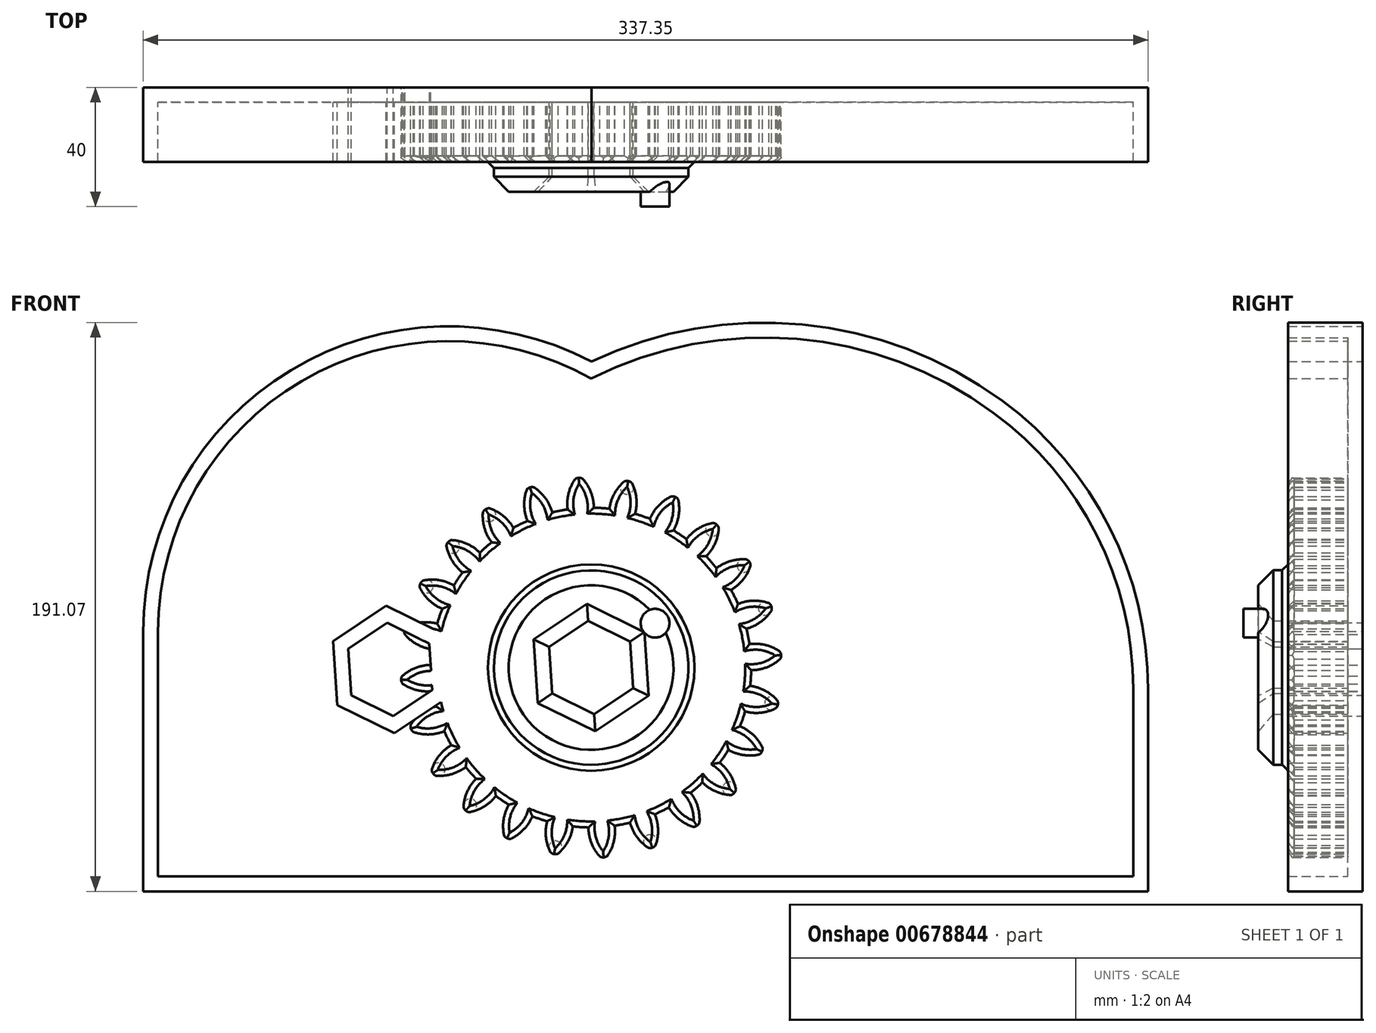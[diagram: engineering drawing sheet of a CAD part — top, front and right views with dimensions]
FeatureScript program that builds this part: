
annotation { "Feature Type Name" : "Feature", "Feature Type Description" : "" }
export const myFeature = defineFeature(function(context is Context, id is Id, definition is map)
    precondition{}
    {
        {
            var Q0;
            Q0=qCreatedBy(makeId("Front.planeOp"),FACE);
            var sketch = newSketch(context, id + "F0", { "sketchPlane" : qUnion([Q0])});
            skCircle(sketch, "E0", {"center": v(0, 0) * mm, "radius": 53.72 * mm});
            skCircle(sketch, "E1", {"center": v(0, 0) * mm, "radius": 58.67 * mm, "construction": true});
            skCircle(sketch, "E2", {"center": v(0, 0) * mm, "radius": 63.5 * mm, "construction": true});
            skLineSegment(sketch, "E3", {"start": v(0, 0) * mm, "end": v(0, 75.2) * mm, "construction": true});
            skLineSegment(sketch, "E4", {"start": v(0, 0) * mm, "end": v(-5.34, 81.5) * mm, "construction": true});
            skLineSegment(sketch, "E5", {"start": v(0, 58.67) * mm, "end": v(-72.87, 58.67) * mm, "construction": true});
            skLineSegment(sketch, "E6", {"start": v(0, 58.67) * mm, "end": v(-71.24, 32.75) * mm, "construction": true});
            skCircle(sketch, "E7", {"center": v(0, 0) * mm, "radius": 55.14 * mm, "construction": true});
            skCircle(sketch, "E8", {"center": v(0, 58.67) * mm, "radius": 14.6 * mm, "construction": true});
            skCircle(sketch, "E9", {"center": v(-13.72, 53.68) * mm, "radius": 14.6 * mm, "construction": true});
            skArc(sketch, "E10", {"start": v(0, 58.67) * mm, "mid": v(-1.2, 61.2) * mm, "end": v(-2.86, 63.44) * mm});
            skArc(sketch, "E11", {"start": v(0.88, 53.71) * mm, "mid": v(0.66, 56.23) * mm, "end": v(0, 58.67) * mm});
            skArc(sketch, "E12.MirrorCS", {"start": v(-7.88, 53.14) * mm, "mid": v(-8, 55.67) * mm, "end": v(-7.66, 58.17) * mm});
            skArc(sketch, "E13.MirrorCS", {"start": v(-7.66, 58.17) * mm, "mid": v(-6.8, 60.82) * mm, "end": v(-5.45, 63.27) * mm});
            skArc(sketch, "E14", {"start": v(-2.86, 63.44) * mm, "mid": v(-4.18, 63.76) * mm, "end": v(-5.45, 63.27) * mm});
            skCircle(sketch, "E15", {"center": v(0, 0) * mm, "radius": 32.66 * mm});
            skCircle(sketch, "E16.cCircle", {"center": v(0, 0) * mm, "radius": 15.7 * mm, "construction": true});
            skLineSegment(sketch, "E16.0", {"start": v(-1.03, 15.66) * mm, "end": v(13.05, 8.72) * mm});
            skLineSegment(sketch, "E16.1", {"start": v(13.05, 8.72) * mm, "end": v(14.08, -6.94) * mm});
            skLineSegment(sketch, "E16.2", {"start": v(14.08, -6.94) * mm, "end": v(1.03, -15.66) * mm});
            skLineSegment(sketch, "E16.3", {"start": v(1.03, -15.66) * mm, "end": v(-13.05, -8.72) * mm});
            skLineSegment(sketch, "E16.4", {"start": v(-13.05, -8.72) * mm, "end": v(-14.08, 6.94) * mm});
            skLineSegment(sketch, "E16.5", {"start": v(-14.08, 6.94) * mm, "end": v(-1.03, 15.66) * mm});
            skSolve(sketch);
        }
        {
            var Q0;
            {var subQ0=sQuery(id+"F0.wireOp",EDGE,"E0");var subQ1=makeQuery(id+"F0.imprint","INTERSECT",VERTEX,{"derivedFrom":[subQ0,sQuery(id+"F0.wireOp",EDGE,"E11")]});Q0=makeQuery(id+"F0.imprint","IMPRINT",FACE,{"disambiguationData":[TD([[makeQuery(id+"F0.imprint","IMPRINT",EDGE,{"disambiguationData":[TD([[subQ1,-1.0]])],"derivedFrom":subQ0}),1.0]])]});}
            var Q1;
            Q1=makeQuery(id+"F0.imprint","IMPRINT",FACE,{"disambiguationData":[TD([[makeQuery(id+"F0.imprint","IMPRINT",EDGE,{"derivedFrom":sQuery(id+"F0.wireOp",EDGE,"E10")}),1.0]])]});
            extrude(context, id + "F1", {"entities" : qUnion([Q0, Q1]), "depth" : 25 * mm, "offsetDistance" : 25 * mm});
        }
        {
            var Q0;
            Q0=makeQuery(id+"F1.opExtrude","SWEPT_BODY",BODY,{"disambiguationData":[OSD([sQuery(id+"F0.wireOp",EDGE,"E0"),sQuery(id+"F0.wireOp",EDGE,"E10"),sQuery(id+"F0.wireOp",EDGE,"E11"),sQuery(id+"F0.wireOp",EDGE,"E12.MirrorCS"),sQuery(id+"F0.wireOp",EDGE,"E13.MirrorCS"),sQuery(id+"F0.wireOp",EDGE,"E14")])]});
            var Q1;
            Q1=makeQuery(id+"F1.opExtrude","SWEPT_FACE",FACE,{"disambiguationData":[OSD([sQuery(id+"F0.wireOp",EDGE,"E0")])]});
            circularPattern(context, id + "F2", {"entities" : qUnion([Q0]), "axis" : qUnion([Q1]), "angle" : 360 * degree, "instanceCount" : 24, "equalSpace" : true});
        }
        {
            var Q0;
            Q0=makeQuery(id+"F0.imprint","IMPRINT",FACE,{"disambiguationData":[TD([[makeQuery(id+"F0.imprint","IMPRINT",EDGE,{"derivedFrom":sQuery(id+"F0.wireOp",EDGE,"E15")}),1.0]])]});
            extrude(context, id + "F3", {"entities" : qUnion([Q0]), "operationType" : NewBodyOperationType.ADD, "depth" : 35 * mm, "offsetDistance" : 25 * mm});
        }
        {
            var Q0;
            Q0=makeQuery(id+"F3.opExtrude","CAP_FACE",FACE,{"disambiguationData":[OSD([sQuery(id+"F0.wireOp",EDGE,"E15"),sQuery(id+"F0.wireOp",EDGE,"E16.0"),sQuery(id+"F0.wireOp",EDGE,"E16.1"),sQuery(id+"F0.wireOp",EDGE,"E16.2"),sQuery(id+"F0.wireOp",EDGE,"E16.3"),sQuery(id+"F0.wireOp",EDGE,"E16.4"),sQuery(id+"F0.wireOp",EDGE,"E16.5")])],"isStart":false});
            chamfer(context, id + "F4", {"entities" : qUnion([Q0]), "width" : 5 * mm, "tangentPropagation" : true});
        }
        {
            var Q0;
            Q0=makeQuery(id+"F2.opPattern","COPY",EDGE,{"derivedFrom":makeQuery(id+"F1.opExtrude","CAP_EDGE",EDGE,{"disambiguationData":[OSD([sQuery(id+"F0.wireOp",EDGE,"E14")])],"isStart":false}),"instanceName":"21"});
            var Q1;
            Q1=makeQuery(id+"F2.opPattern","COPY",EDGE,{"derivedFrom":makeQuery(id+"F1.opExtrude","CAP_EDGE",EDGE,{"disambiguationData":[OSD([sQuery(id+"F0.wireOp",EDGE,"E10")])],"isStart":false}),"instanceName":"21"});
            var Q2;
            Q2=makeQuery(id+"F2.opPattern","COPY",EDGE,{"derivedFrom":makeQuery(id+"F1.opExtrude","CAP_EDGE",EDGE,{"disambiguationData":[OSD([sQuery(id+"F0.wireOp",EDGE,"E11")])],"isStart":false}),"instanceName":"21"});
            var Q3;
            Q3=makeQuery(id+"F2.opPattern","COPY",EDGE,{"derivedFrom":makeQuery(id+"F1.opExtrude","CAP_EDGE",EDGE,{"disambiguationData":[OSD([sQuery(id+"F0.wireOp",EDGE,"E13.MirrorCS")])],"isStart":false}),"instanceName":"21"});
            var Q4;
            Q4=makeQuery(id+"F2.opPattern","COPY",EDGE,{"derivedFrom":makeQuery(id+"F1.opExtrude","CAP_EDGE",EDGE,{"disambiguationData":[OSD([sQuery(id+"F0.wireOp",EDGE,"E12.MirrorCS")])],"isStart":false}),"instanceName":"21"});
            var Q5;
            Q5=makeQuery(id+"F1.opExtrude","CAP_EDGE",EDGE,{"disambiguationData":[OSD([sQuery(id+"F0.wireOp",EDGE,"E14")])],"isStart":false});
            var Q6;
            Q6=makeQuery(id+"F1.opExtrude","CAP_EDGE",EDGE,{"disambiguationData":[OSD([sQuery(id+"F0.wireOp",EDGE,"E13.MirrorCS")])],"isStart":false});
            var Q7;
            Q7=makeQuery(id+"F1.opExtrude","CAP_EDGE",EDGE,{"disambiguationData":[OSD([sQuery(id+"F0.wireOp",EDGE,"E10")])],"isStart":false});
            var Q8;
            Q8=makeQuery(id+"F1.opExtrude","CAP_EDGE",EDGE,{"disambiguationData":[OSD([sQuery(id+"F0.wireOp",EDGE,"E12.MirrorCS")])],"isStart":false});
            var Q9;
            Q9=makeQuery(id+"F1.opExtrude","CAP_EDGE",EDGE,{"disambiguationData":[OSD([sQuery(id+"F0.wireOp",EDGE,"E11")])],"isStart":false});
            var Q10;
            Q10=makeQuery(id+"F2.opPattern","COPY",EDGE,{"derivedFrom":makeQuery(id+"F1.opExtrude","CAP_EDGE",EDGE,{"disambiguationData":[OSD([sQuery(id+"F0.wireOp",EDGE,"E13.MirrorCS")])],"isStart":false}),"instanceName":"22"});
            var Q11;
            Q11=makeQuery(id+"F2.opPattern","COPY",EDGE,{"derivedFrom":makeQuery(id+"F1.opExtrude","CAP_EDGE",EDGE,{"disambiguationData":[OSD([sQuery(id+"F0.wireOp",EDGE,"E14")])],"isStart":false}),"instanceName":"22"});
            var Q12;
            Q12=makeQuery(id+"F2.opPattern","COPY",EDGE,{"derivedFrom":makeQuery(id+"F1.opExtrude","CAP_EDGE",EDGE,{"disambiguationData":[OSD([sQuery(id+"F0.wireOp",EDGE,"E12.MirrorCS")])],"isStart":false}),"instanceName":"22"});
            var Q13;
            Q13=makeQuery(id+"F2.opPattern","COPY",EDGE,{"derivedFrom":makeQuery(id+"F1.opExtrude","CAP_EDGE",EDGE,{"disambiguationData":[OSD([sQuery(id+"F0.wireOp",EDGE,"E10")])],"isStart":false}),"instanceName":"22"});
            var Q14;
            Q14=makeQuery(id+"F2.opPattern","COPY",EDGE,{"derivedFrom":makeQuery(id+"F1.opExtrude","CAP_EDGE",EDGE,{"disambiguationData":[OSD([sQuery(id+"F0.wireOp",EDGE,"E11")])],"isStart":false}),"instanceName":"22"});
            var Q15;
            Q15=makeQuery(id+"F2.opPattern","COPY",EDGE,{"derivedFrom":makeQuery(id+"F1.opExtrude","CAP_EDGE",EDGE,{"disambiguationData":[OSD([sQuery(id+"F0.wireOp",EDGE,"E13.MirrorCS")])],"isStart":false}),"instanceName":"23"});
            var Q16;
            Q16=makeQuery(id+"F2.opPattern","COPY",EDGE,{"derivedFrom":makeQuery(id+"F1.opExtrude","CAP_EDGE",EDGE,{"disambiguationData":[OSD([sQuery(id+"F0.wireOp",EDGE,"E14")])],"isStart":false}),"instanceName":"23"});
            var Q17;
            Q17=makeQuery(id+"F2.opPattern","COPY",EDGE,{"derivedFrom":makeQuery(id+"F1.opExtrude","CAP_EDGE",EDGE,{"disambiguationData":[OSD([sQuery(id+"F0.wireOp",EDGE,"E10")])],"isStart":false}),"instanceName":"23"});
            var Q18;
            Q18=makeQuery(id+"F2.opPattern","COPY",EDGE,{"derivedFrom":makeQuery(id+"F1.opExtrude","CAP_EDGE",EDGE,{"disambiguationData":[OSD([sQuery(id+"F0.wireOp",EDGE,"E11")])],"isStart":false}),"instanceName":"23"});
            var Q19;
            Q19=makeQuery(id+"F2.opPattern","COPY",EDGE,{"derivedFrom":makeQuery(id+"F1.opExtrude","CAP_EDGE",EDGE,{"disambiguationData":[OSD([sQuery(id+"F0.wireOp",EDGE,"E12.MirrorCS")])],"isStart":false}),"instanceName":"23"});
            var Q20;
            Q20=makeQuery(id+"F2.opPattern","COPY",EDGE,{"derivedFrom":makeQuery(id+"F1.opExtrude","CAP_EDGE",EDGE,{"disambiguationData":[OSD([sQuery(id+"F0.wireOp",EDGE,"E14")])],"isStart":false}),"instanceName":"20"});
            var Q21;
            Q21=makeQuery(id+"F2.opPattern","COPY",EDGE,{"derivedFrom":makeQuery(id+"F1.opExtrude","CAP_EDGE",EDGE,{"disambiguationData":[OSD([sQuery(id+"F0.wireOp",EDGE,"E10")])],"isStart":false}),"instanceName":"20"});
            var Q22;
            Q22=makeQuery(id+"F2.opPattern","COPY",EDGE,{"derivedFrom":makeQuery(id+"F1.opExtrude","CAP_EDGE",EDGE,{"disambiguationData":[OSD([sQuery(id+"F0.wireOp",EDGE,"E11")])],"isStart":false}),"instanceName":"20"});
            var Q23;
            Q23=makeQuery(id+"F2.opPattern","COPY",EDGE,{"derivedFrom":makeQuery(id+"F1.opExtrude","CAP_EDGE",EDGE,{"disambiguationData":[OSD([sQuery(id+"F0.wireOp",EDGE,"E13.MirrorCS")])],"isStart":false}),"instanceName":"20"});
            var Q24;
            Q24=makeQuery(id+"F2.opPattern","COPY",EDGE,{"derivedFrom":makeQuery(id+"F1.opExtrude","CAP_EDGE",EDGE,{"disambiguationData":[OSD([sQuery(id+"F0.wireOp",EDGE,"E12.MirrorCS")])],"isStart":false}),"instanceName":"20"});
            var Q25;
            Q25=makeQuery(id+"F2.opPattern","COPY",EDGE,{"derivedFrom":makeQuery(id+"F1.opExtrude","CAP_EDGE",EDGE,{"disambiguationData":[OSD([sQuery(id+"F0.wireOp",EDGE,"E10")])],"isStart":false}),"instanceName":"19"});
            var Q26;
            Q26=makeQuery(id+"F2.opPattern","COPY",EDGE,{"derivedFrom":makeQuery(id+"F1.opExtrude","CAP_EDGE",EDGE,{"disambiguationData":[OSD([sQuery(id+"F0.wireOp",EDGE,"E11")])],"isStart":false}),"instanceName":"19"});
            var Q27;
            Q27=makeQuery(id+"F2.opPattern","COPY",EDGE,{"derivedFrom":makeQuery(id+"F1.opExtrude","CAP_EDGE",EDGE,{"disambiguationData":[OSD([sQuery(id+"F0.wireOp",EDGE,"E14")])],"isStart":false}),"instanceName":"19"});
            var Q28;
            Q28=makeQuery(id+"F2.opPattern","COPY",EDGE,{"derivedFrom":makeQuery(id+"F1.opExtrude","CAP_EDGE",EDGE,{"disambiguationData":[OSD([sQuery(id+"F0.wireOp",EDGE,"E13.MirrorCS")])],"isStart":false}),"instanceName":"19"});
            var Q29;
            Q29=makeQuery(id+"F2.opPattern","COPY",EDGE,{"derivedFrom":makeQuery(id+"F1.opExtrude","CAP_EDGE",EDGE,{"disambiguationData":[OSD([sQuery(id+"F0.wireOp",EDGE,"E12.MirrorCS")])],"isStart":false}),"instanceName":"19"});
            var Q30;
            Q30=makeQuery(id+"F2.opPattern","COPY",EDGE,{"derivedFrom":makeQuery(id+"F1.opExtrude","CAP_EDGE",EDGE,{"disambiguationData":[OSD([sQuery(id+"F0.wireOp",EDGE,"E14")])],"isStart":false}),"instanceName":"18"});
            var Q31;
            Q31=makeQuery(id+"F2.opPattern","COPY",EDGE,{"derivedFrom":makeQuery(id+"F1.opExtrude","CAP_EDGE",EDGE,{"disambiguationData":[OSD([sQuery(id+"F0.wireOp",EDGE,"E13.MirrorCS")])],"isStart":false}),"instanceName":"18"});
            var Q32;
            Q32=makeQuery(id+"F2.opPattern","COPY",EDGE,{"derivedFrom":makeQuery(id+"F1.opExtrude","CAP_EDGE",EDGE,{"disambiguationData":[OSD([sQuery(id+"F0.wireOp",EDGE,"E12.MirrorCS")])],"isStart":false}),"instanceName":"18"});
            var Q33;
            Q33=makeQuery(id+"F2.opPattern","COPY",EDGE,{"derivedFrom":makeQuery(id+"F1.opExtrude","CAP_EDGE",EDGE,{"disambiguationData":[OSD([sQuery(id+"F0.wireOp",EDGE,"E10")])],"isStart":false}),"instanceName":"18"});
            var Q34;
            {var subQ0=makeQuery(id+"F1.opExtrude","CAP_FACE",FACE,{"disambiguationData":[OSD([sQuery(id+"F0.wireOp",EDGE,"E0"),sQuery(id+"F0.wireOp",EDGE,"E10"),sQuery(id+"F0.wireOp",EDGE,"E11"),sQuery(id+"F0.wireOp",EDGE,"E12.MirrorCS"),sQuery(id+"F0.wireOp",EDGE,"E13.MirrorCS"),sQuery(id+"F0.wireOp",EDGE,"E14"),sQuery(id+"F0.wireOp",EDGE,"E15")])],"isStart":false});Q34=makeQuery(id+"F3.boolean.opBoolean","MERGE",FACE,{"derivedFrom":[subQ0,makeQuery(id+"F2.opPattern","COPY",FACE,{"derivedFrom":subQ0,"instanceName":"1"}),makeQuery(id+"F2.opPattern","COPY",FACE,{"derivedFrom":subQ0,"instanceName":"2"}),makeQuery(id+"F2.opPattern","COPY",FACE,{"derivedFrom":subQ0,"instanceName":"3"}),makeQuery(id+"F2.opPattern","COPY",FACE,{"derivedFrom":subQ0,"instanceName":"4"}),makeQuery(id+"F2.opPattern","COPY",FACE,{"derivedFrom":subQ0,"instanceName":"5"}),makeQuery(id+"F2.opPattern","COPY",FACE,{"derivedFrom":subQ0,"instanceName":"6"}),makeQuery(id+"F2.opPattern","COPY",FACE,{"derivedFrom":subQ0,"instanceName":"7"}),makeQuery(id+"F2.opPattern","COPY",FACE,{"derivedFrom":subQ0,"instanceName":"8"}),makeQuery(id+"F2.opPattern","COPY",FACE,{"derivedFrom":subQ0,"instanceName":"9"}),makeQuery(id+"F2.opPattern","COPY",FACE,{"derivedFrom":subQ0,"instanceName":"10"}),makeQuery(id+"F2.opPattern","COPY",FACE,{"derivedFrom":subQ0,"instanceName":"11"}),makeQuery(id+"F2.opPattern","COPY",FACE,{"derivedFrom":subQ0,"instanceName":"12"}),makeQuery(id+"F2.opPattern","COPY",FACE,{"derivedFrom":subQ0,"instanceName":"13"}),makeQuery(id+"F2.opPattern","COPY",FACE,{"derivedFrom":subQ0,"instanceName":"14"}),makeQuery(id+"F2.opPattern","COPY",FACE,{"derivedFrom":subQ0,"instanceName":"15"}),makeQuery(id+"F2.opPattern","COPY",FACE,{"derivedFrom":subQ0,"instanceName":"16"}),makeQuery(id+"F2.opPattern","COPY",FACE,{"derivedFrom":subQ0,"instanceName":"17"}),makeQuery(id+"F2.opPattern","COPY",FACE,{"derivedFrom":subQ0,"instanceName":"18"}),makeQuery(id+"F2.opPattern","COPY",FACE,{"derivedFrom":subQ0,"instanceName":"19"}),makeQuery(id+"F2.opPattern","COPY",FACE,{"derivedFrom":subQ0,"instanceName":"20"}),makeQuery(id+"F2.opPattern","COPY",FACE,{"derivedFrom":subQ0,"instanceName":"21"}),makeQuery(id+"F2.opPattern","COPY",FACE,{"derivedFrom":subQ0,"instanceName":"22"}),makeQuery(id+"F2.opPattern","COPY",FACE,{"derivedFrom":subQ0,"instanceName":"23"})]});}
            chamfer(context, id + "F5", {"entities" : qUnion([Q0, Q1, Q2, Q3, Q4, Q5, Q6, Q7, Q8, Q9, Q10, Q11, Q12, Q13, Q14, Q15, Q16, Q17, Q18, Q19, Q20, Q21, Q22, Q23, Q24, Q25, Q26, Q27, Q28, Q29, Q30, Q31, Q32, Q33, Q34]), "width" : 2 * mm, "tangentPropagation" : true});
        }
        {
            var Q0;
            Q0=qCreatedBy(makeId("Front.planeOp"),FACE);
            var sketch = newSketch(context, id + "F6", { "sketchPlane" : qUnion([Q0])});
            skLineSegment(sketch, "E17", {"start": v(-150.39, -75.18) * mm, "end": v(186.96, -75.18) * mm});
            skLineSegment(sketch, "E18", {"start": v(186.96, -75.18) * mm, "end": v(186.96, -7.21) * mm});
            skLineSegment(sketch, "E19", {"start": v(-150.39, -75.18) * mm, "end": v(-150.39, 12.08) * mm});
            skArc(sketch, "E20", {"start": v(0.07, 102.78) * mm, "mid": v(-100.77, 99.92) * mm, "end": v(-150.39, 12.08) * mm});
            skArc(sketch, "E21", {"start": v(138, 89.63) * mm, "mid": v(70.85, 115.28) * mm, "end": v(0.07, 102.78) * mm});
            skArc(sketch, "E22", {"start": v(186.96, -7.21) * mm, "mid": v(174.02, 47.05) * mm, "end": v(138, 89.63) * mm});
            skLineSegment(sketch, "E23.0", {"start": v(-68.45, 15.02) * mm, "end": v(-54.37, 8.07) * mm});
            skLineSegment(sketch, "E23.1", {"start": v(-54.37, 8.07) * mm, "end": v(-53.34, -7.6) * mm});
            skLineSegment(sketch, "E23.2", {"start": v(-53.34, -7.6) * mm, "end": v(-66.4, -16.31) * mm});
            skLineSegment(sketch, "E23.3", {"start": v(-66.4, -16.31) * mm, "end": v(-80.47, -9.37) * mm});
            skLineSegment(sketch, "E23.4", {"start": v(-80.47, -9.37) * mm, "end": v(-81.5, 6.3) * mm});
            skLineSegment(sketch, "E23.5", {"start": v(-81.5, 6.3) * mm, "end": v(-68.45, 15.02) * mm});
            skSolve(sketch);
        }
        {
            var Q0;
            Q0=makeQuery(id+"F6.imprint","IMPRINT",FACE,{"disambiguationData":[TD([[makeQuery(id+"F6.imprint","IMPRINT",EDGE,{"derivedFrom":sQuery(id+"F6.wireOp",EDGE,"E17")}),1.0]])]});
            extrude(context, id + "F7", {"entities" : qUnion([Q0]), "depth" : 25 * mm, "offsetDistance" : 25 * mm});
        }
        {
            var Q0;
            Q0=makeQuery(id+"F7.opExtrude","CAP_FACE",FACE,{"disambiguationData":[OSD([sQuery(id+"F6.wireOp",EDGE,"E17"),sQuery(id+"F6.wireOp",EDGE,"E18"),sQuery(id+"F6.wireOp",EDGE,"E19"),sQuery(id+"F6.wireOp",EDGE,"E20"),sQuery(id+"F6.wireOp",EDGE,"E21"),sQuery(id+"F6.wireOp",EDGE,"E22")])],"isStart":false});
            shell(context, id + "F8", {"entities" : qUnion([Q0]), "thickness" : 5 * mm});
        }
        {
            var Q0;
            Q0=makeQuery(id+"F7.opExtrude","CAP_FACE",FACE,{"disambiguationData":[OSD([sQuery(id+"F6.wireOp",EDGE,"E17"),sQuery(id+"F6.wireOp",EDGE,"E18"),sQuery(id+"F6.wireOp",EDGE,"E19"),sQuery(id+"F6.wireOp",EDGE,"E20"),sQuery(id+"F6.wireOp",EDGE,"E21"),sQuery(id+"F6.wireOp",EDGE,"E22"),sQuery(id+"F6.wireOp",EDGE,"294d7e43-28af-494b-8422-083210c35582.0"),sQuery(id+"F6.wireOp",EDGE,"294d7e43-28af-494b-8422-083210c35582.1"),sQuery(id+"F6.wireOp",EDGE,"294d7e43-28af-494b-8422-083210c35582.2"),sQuery(id+"F6.wireOp",EDGE,"294d7e43-28af-494b-8422-083210c35582.3"),sQuery(id+"F6.wireOp",EDGE,"294d7e43-28af-494b-8422-083210c35582.4"),sQuery(id+"F6.wireOp",EDGE,"294d7e43-28af-494b-8422-083210c35582.5")])],"isStart":false});
            extrude(context, id + "F9", {"entities" : qUnion([Q0]), "operationType" : NewBodyOperationType.REMOVE, "depth" : 25 * mm, "offsetDistance" : 25 * mm});
        }
        {
            var Q0;
            {var subQ0=sQuery(id+"F6.wireOp",EDGE,"E23.5");var subQ1=sQuery(id+"F6.wireOp",EDGE,"E23.4");var subQ2=sQuery(id+"F6.wireOp",EDGE,"E23.3");var subQ3=sQuery(id+"F6.wireOp",EDGE,"E23.2");var subQ4=sQuery(id+"F6.wireOp",EDGE,"E23.1");var subQ5=sQuery(id+"F6.wireOp",EDGE,"E23.0");var subQ6=sQuery(id+"F6.wireOp",EDGE,"E22");var subQ7=sQuery(id+"F6.wireOp",EDGE,"E21");var subQ8=sQuery(id+"F6.wireOp",EDGE,"E20");var subQ9=sQuery(id+"F6.wireOp",EDGE,"E19");var subQ10=sQuery(id+"F6.wireOp",EDGE,"E18");var subQ11=sQuery(id+"F6.wireOp",EDGE,"E17");Q0=makeQuery(id+"F8.opShell","OFFSET_FACE",FACE,{"disambiguationData":[OSD([subQ11,subQ10,subQ9,subQ8,subQ7,subQ6,subQ5,subQ4,subQ3,subQ2,subQ1,subQ0]),TDD([makeQuery(id+"F7.opExtrude","CAP_FACE",FACE,{"disambiguationData":[OSD([subQ11,subQ10,subQ9,subQ8,subQ7,subQ6,subQ5,subQ4,subQ3,subQ2,subQ1,subQ0])],"isStart":true})])]});}
            var sketch = newSketch(context, id + "F10", { "sketchPlane" : qUnion([Q0])});
            skCircle(sketch, "E24", {"center": v(21.46, 14.9) * mm, "radius": 4.82 * mm});
            skSolve(sketch);
        }
        {
            var Q0;
            Q0=makeQuery(id+"F10.imprint","IMPRINT",FACE,{"disambiguationData":[TD([[makeQuery(id+"F10.imprint","IMPRINT",EDGE,{"derivedFrom":sQuery(id+"F10.wireOp",EDGE,"E24")}),1.0]])]});
            extrude(context, id + "F11", {"entities" : qUnion([Q0]), "operationType" : NewBodyOperationType.ADD, "depth" : 35 * mm, "offsetDistance" : 25 * mm});
        }
    });
